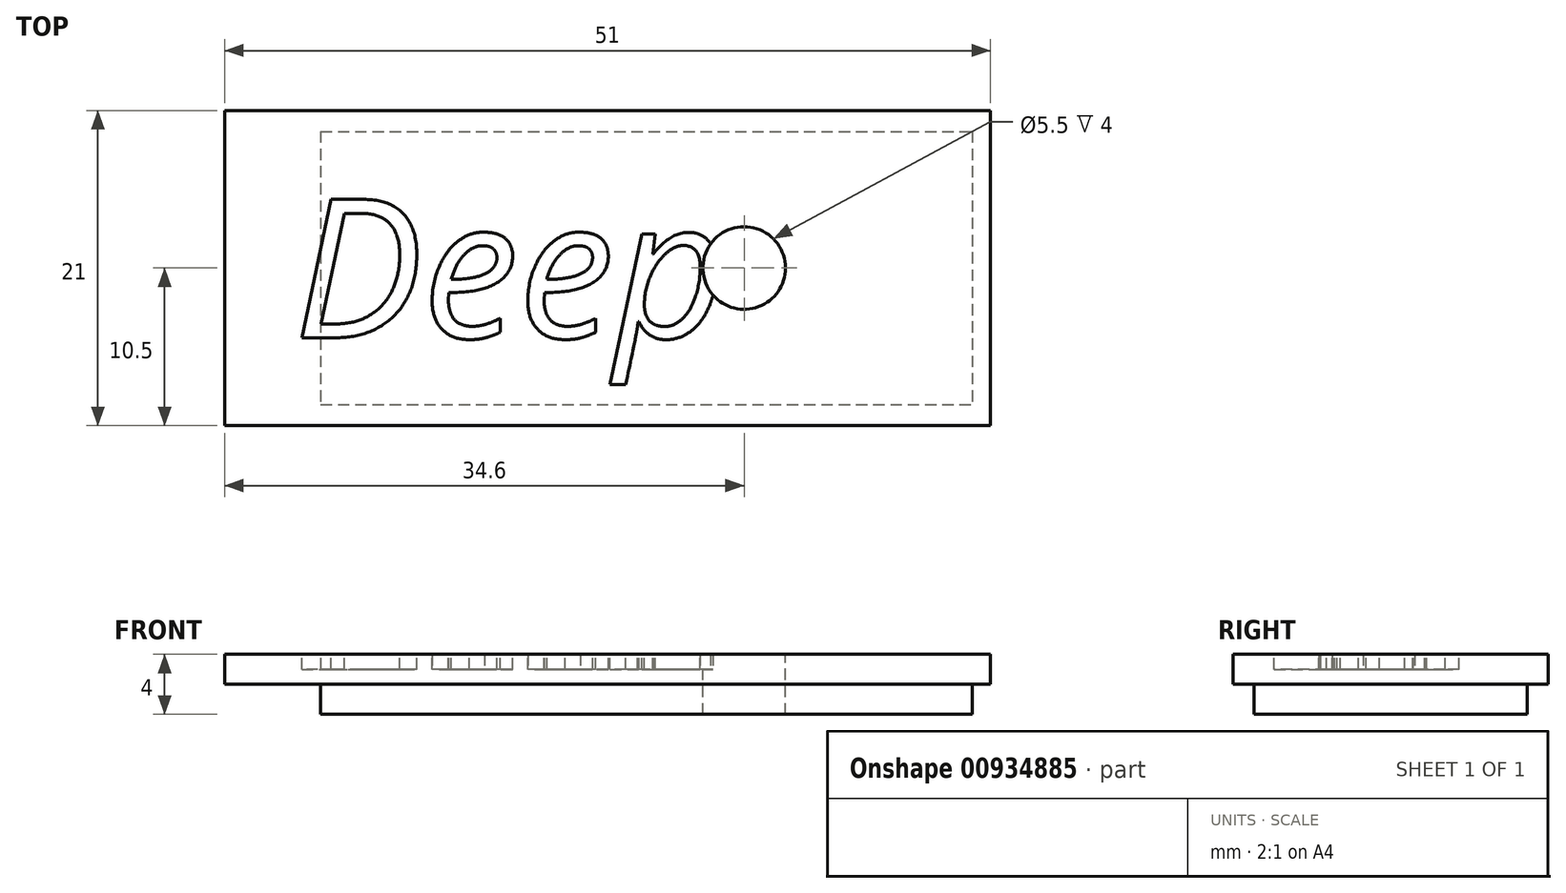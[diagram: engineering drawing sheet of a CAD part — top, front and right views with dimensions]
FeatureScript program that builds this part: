
annotation { "Feature Type Name" : "Feature", "Feature Type Description" : "" }
export const myFeature = defineFeature(function(context is Context, id is Id, definition is map)
    precondition{}
    {
        {
            var Q0;
            Q0=qCreatedBy(makeId("Top.planeOp"),FACE);
            var sketch = newSketch(context, id + "F0", { "sketchPlane" : qUnion([Q0])});
            skLineSegment(sketch, "E0.bottom", {"start": v(-21.7, 9.1) * mm, "end": v(21.7, 9.1) * mm});
            skLineSegment(sketch, "E0.top", {"start": v(-21.7, -9.1) * mm, "end": v(21.7, -9.1) * mm});
            skLineSegment(sketch, "E0.left", {"start": v(-21.7, 9.1) * mm, "end": v(-21.7, -9.1) * mm});
            skLineSegment(sketch, "E0.right", {"start": v(21.7, 9.1) * mm, "end": v(21.7, -9.1) * mm});
            skSolve(sketch);
        }
        {
            var Q0;
            Q0=makeQuery(id+"F0.imprint","IMPRINT",FACE,{"disambiguationData":[TD([[makeQuery(id+"F0.imprint","IMPRINT",EDGE,{"derivedFrom":sQuery(id+"F0.wireOp",EDGE,"E0.bottom")}),-1.0]])]});
            extrude(context, id + "F1", {"entities" : qUnion([Q0]), "depth" : 2 * mm, "offsetDistance" : 25 * mm});
        }
        {
            var Q0;
            Q0=makeQuery(id+"F1.opExtrude","CAP_FACE",FACE,{"disambiguationData":[OSD([sQuery(id+"F0.wireOp",EDGE,"E0.bottom"),sQuery(id+"F0.wireOp",EDGE,"E0.top"),sQuery(id+"F0.wireOp",EDGE,"E0.left"),sQuery(id+"F0.wireOp",EDGE,"E0.right")])],"isStart":false});
            var sketch = newSketch(context, id + "F2", { "sketchPlane" : qUnion([Q0])});
            skLineSegment(sketch, "E1.bottom", {"start": v(-28.1, 10.5) * mm, "end": v(22.9, 10.5) * mm});
            skLineSegment(sketch, "E1.top", {"start": v(-28.1, -10.5) * mm, "end": v(22.9, -10.5) * mm});
            skLineSegment(sketch, "E1.left", {"start": v(-28.1, 10.5) * mm, "end": v(-28.1, -10.5) * mm});
            skLineSegment(sketch, "E1.right", {"start": v(22.9, 10.5) * mm, "end": v(22.9, -10.5) * mm});
            skLineSegment(sketch, "E2.bottom", {"start": v(22.09, 10.5) * mm, "end": v(23.58, 10.5) * mm});
            skLineSegment(sketch, "E2.top", {"start": v(23.98, 0) * mm, "end": v(25.47, 0) * mm});
            skSolve(sketch);
        }
        {
            var Q0;
            Q0=makeQuery(id+"F2.imprint","IMPRINT",FACE,{"disambiguationData":[TD([[makeQuery(id+"F2.imprint","IMPRINT",EDGE,{"derivedFrom":makeQuery(id+"F1.opExtrude","CAP_EDGE",EDGE,{"disambiguationData":[OSD([sQuery(id+"F0.wireOp",EDGE,"E0.bottom")])],"isStart":false})}),-1.0]])]});
            var Q1;
            Q1=makeQuery(id+"F2.imprint","IMPRINT",FACE,{"disambiguationData":[TD([[makeQuery(id+"F2.imprint","IMPRINT",EDGE,{"derivedFrom":sQuery(id+"F2.wireOp",EDGE,"E1.top")}),1.0]])]});
            extrude(context, id + "F3", {"entities" : qUnion([Q0, Q1]), "operationType" : NewBodyOperationType.ADD, "depth" : 2 * mm, "offsetDistance" : 25 * mm});
        }
        {
            var Q0;
            Q0=makeQuery(id+"F3.opExtrude","CAP_FACE",FACE,{"disambiguationData":[OSD([sQuery(id+"F2.wireOp",EDGE,"E1.bottom"),sQuery(id+"F2.wireOp",EDGE,"E1.top"),sQuery(id+"F2.wireOp",EDGE,"E1.left"),sQuery(id+"F2.wireOp",EDGE,"E1.right"),sQuery(id+"F2.wireOp",EDGE,"E2.bottom")])],"isStart":false});
            var sketch = newSketch(context, id + "F4", { "sketchPlane" : qUnion([Q0])});
            skCircle(sketch, "E3", {"center": v(6.5, 0) * mm, "radius": 2.75 * mm});
            skSolve(sketch);
        }
        {
            var Q0;
            Q0=makeQuery(id+"F4.imprint","IMPRINT",FACE,{"disambiguationData":[TD([[makeQuery(id+"F4.imprint","IMPRINT",EDGE,{"derivedFrom":sQuery(id+"F4.wireOp",EDGE,"E3")}),1.0]])]});
            extrude(context, id + "F5", {"entities" : qUnion([Q0]), "operationType" : NewBodyOperationType.REMOVE, "endBound" : BoundingType.UP_TO_NEXT, "oppositeDirection" : true, "depth" : 25 * mm, "offsetDistance" : 25 * mm});
        }
        {
            var Q0;
            Q0=makeQuery(id+"F3.opExtrude","CAP_FACE",FACE,{"disambiguationData":[OSD([sQuery(id+"F2.wireOp",EDGE,"E1.bottom"),sQuery(id+"F2.wireOp",EDGE,"E1.top"),sQuery(id+"F2.wireOp",EDGE,"E1.left"),sQuery(id+"F2.wireOp",EDGE,"E1.right"),sQuery(id+"F2.wireOp",EDGE,"E2.bottom")])],"isStart":false});
            var sketch = newSketch(context, id + "F6", { "sketchPlane" : qUnion([Q0])});
            skText(sketch, "E4", { "text": "Deep", "fontName": "OpenSans-Italic.ttf"});
            const initialGuessF6  = {"E4": [-0.0235, -0.00465, 1, 0, 0.0093]};
            skSetInitialGuess(sketch, initialGuessF6);
            skSolve(sketch);
        }
        {
            var Q0;
            Q0 = qSketchRegion(id + "F6", true);
            extrude(context, id + "F7", {"entities" : qUnion([Q0]), "operationType" : NewBodyOperationType.REMOVE, "oppositeDirection" : true, "depth" : 1 * mm, "offsetDistance" : 25 * mm});
        }
    });
